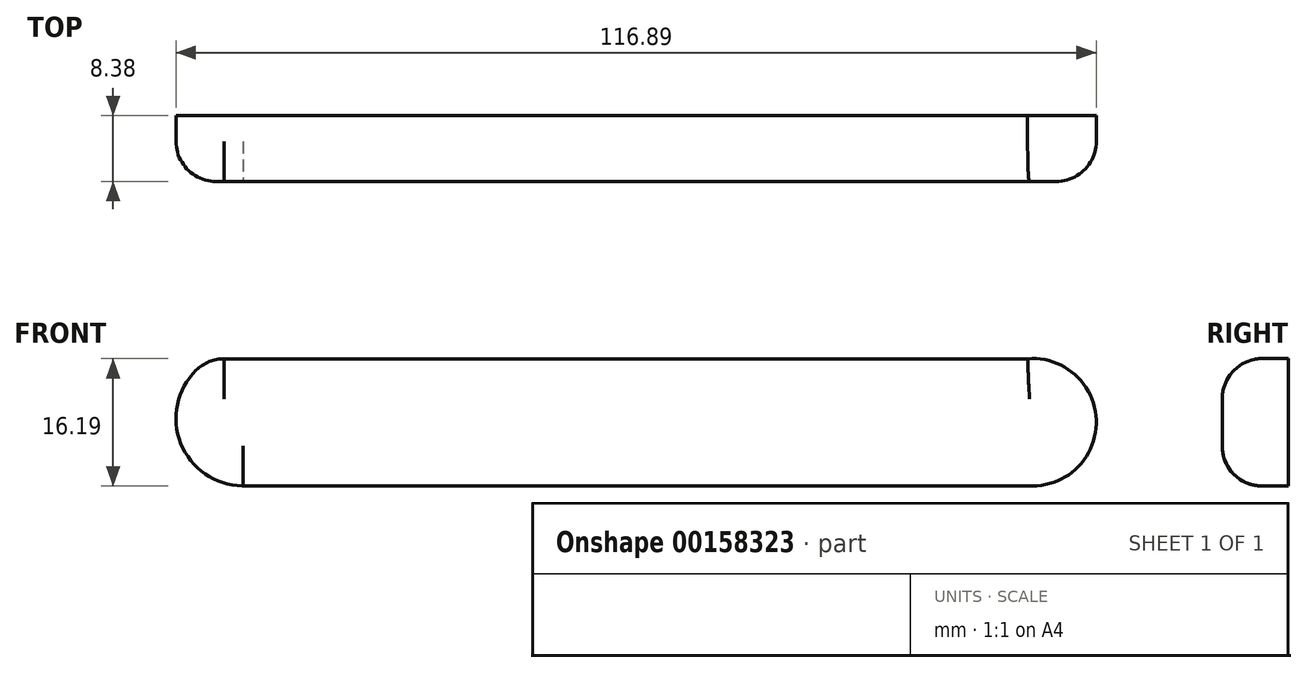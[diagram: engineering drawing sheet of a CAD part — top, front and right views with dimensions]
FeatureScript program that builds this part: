
annotation { "Feature Type Name" : "Feature", "Feature Type Description" : "" }
export const myFeature = defineFeature(function(context is Context, id is Id, definition is map)
    precondition{}
    {
        {
            var Q0;
            Q0=qCreatedBy(makeId("Front.planeOp"),FACE);
            var sketch = newSketch(context, id + "F0", { "sketchPlane" : qUnion([Q0])});
            skArc(sketch, "E0", {"start": v(-36.68, 10.82) * mm, "mid": v(-40.99, 1.22) * mm, "end": v(-32.76, -5.35) * mm});
            skLineSegment(sketch, "E1", {"start": v(-36.68, 10.82) * mm, "end": v(66.95, 10.82) * mm});
            skLineSegment(sketch, "E2", {"start": v(-32.76, -5.35) * mm, "end": v(67.57, -5.35) * mm});
            skArc(sketch, "E3", {"start": v(67.57, -5.35) * mm, "mid": v(75.66, 3.06) * mm, "end": v(66.95, 10.82) * mm});
            skSolve(sketch);
        }
        {
            var Q0;
            Q0 = qSketchRegion(id + "F0", true);
            extrude(context, id + "F1", {"entities" : qUnion([Q0]), "depth" : 8.38 * mm});
        }
        {
            var Q0;
            Q0=makeQuery(id+"F1.opExtrude","CAP_EDGE",EDGE,{"disambiguationData":[OSD([sQuery(id+"F0.wireOp",EDGE,"E1")])],"isStart":false});
            var Q1;
            Q1=makeQuery(id+"F1.opExtrude","CAP_EDGE",EDGE,{"disambiguationData":[OSD([sQuery(id+"F0.wireOp",EDGE,"E2")])],"isStart":false});
            fillet(context, id + "F2", {"entities" : qUnion([Q0, Q1]), "radius" : 5.08 * mm, "tangentPropagation" : true, "allowEdgeOverflow" : false});
        }
        {
            var Q0;
            Q0=makeQuery(id+"F1.opExtrude","CAP_EDGE",EDGE,{"disambiguationData":[OSD([sQuery(id+"F0.wireOp",EDGE,"E0")])],"isStart":false});
            fillet(context, id + "F3", {"entities" : qUnion([Q0]), "radius" : 5.08 * mm, "tangentPropagation" : true, "allowEdgeOverflow" : false});
        }
    });
